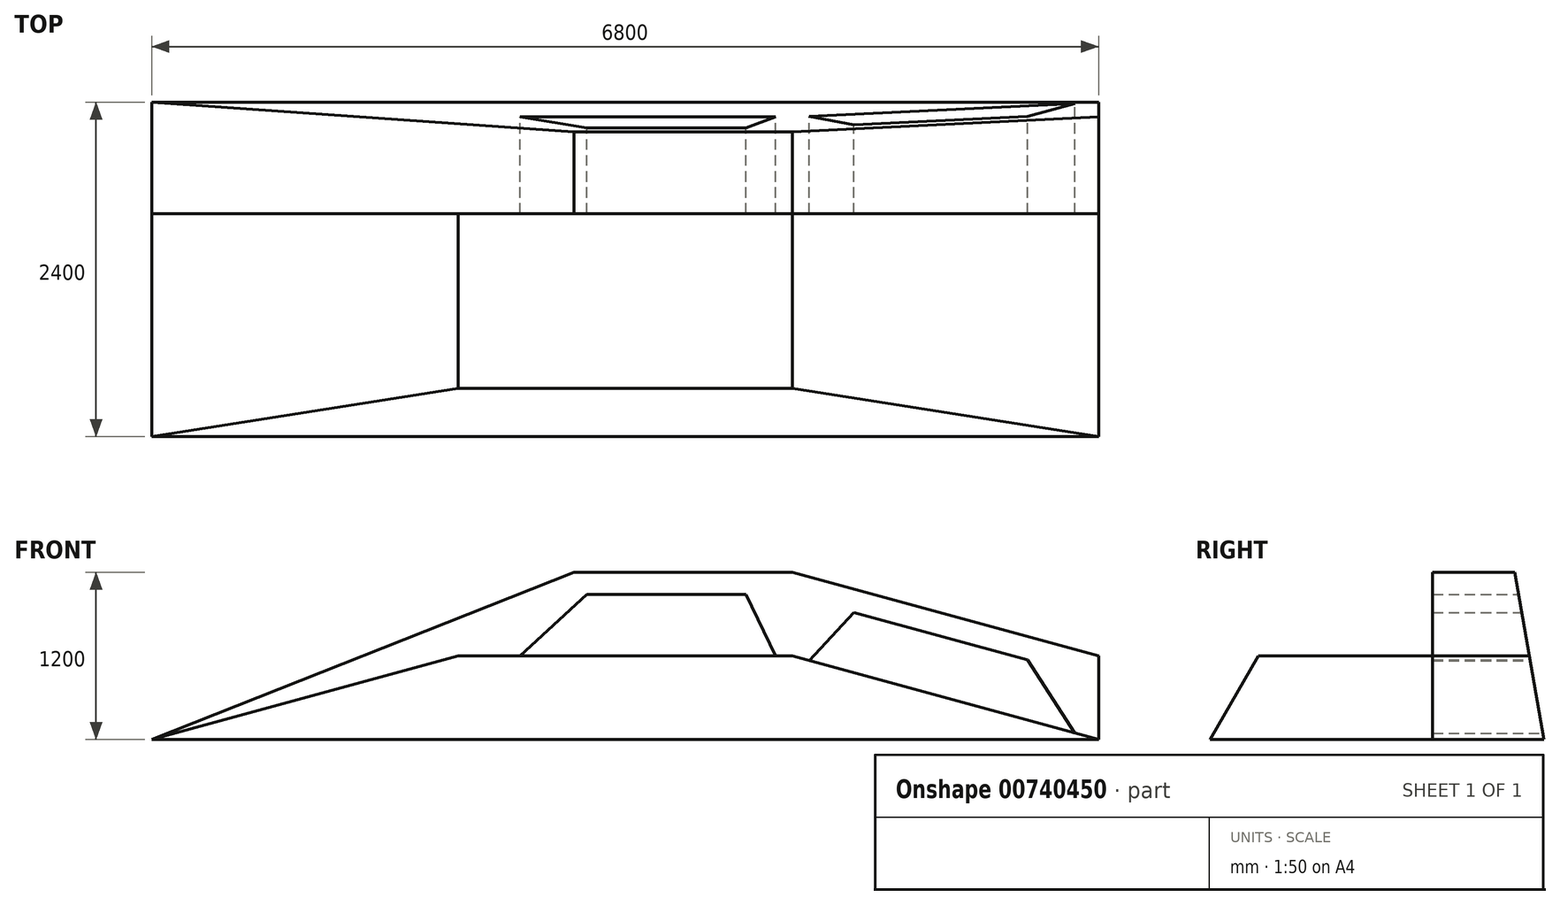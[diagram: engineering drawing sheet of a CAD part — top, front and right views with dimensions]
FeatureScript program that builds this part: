
annotation { "Feature Type Name" : "Feature", "Feature Type Description" : "" }
export const myFeature = defineFeature(function(context is Context, id is Id, definition is map)
    precondition{}
    {
        {
            var Q0;
            Q0=qCreatedBy(makeId("Top.planeOp"),FACE);
            var sketch = newSketch(context, id + "F0", { "sketchPlane" : qUnion([Q0])});
            skLineSegment(sketch, "E0.bottom", {"start": v(3400, 1200) * mm, "end": v(-3400, 1200) * mm});
            skLineSegment(sketch, "E0.top", {"start": v(3400, -1200) * mm, "end": v(-3400, -1200) * mm});
            skLineSegment(sketch, "E0.left", {"start": v(3400, 1200) * mm, "end": v(3400, -1200) * mm});
            skLineSegment(sketch, "E0.right", {"start": v(-3400, 1200) * mm, "end": v(-3400, -1200) * mm});
            skPoint(sketch, "E0.middle", {"position": v(0, 0) * mm});
            skSolve(sketch);
        }
        {
            var Q0;
            Q0=qCreatedBy(makeId("Front.planeOp"),FACE);
            var sketch = newSketch(context, id + "F1", { "sketchPlane" : qUnion([Q0])});
            skPoint(sketch, "E1.orphan", {"position": v(0, 354.61) * mm});
            skLineSegment(sketch, "E2", {"start": v(3400, 0) * mm, "end": v(-3400, 0) * mm});
            skLineSegment(sketch, "E3.MirrorCS", {"start": v(0, 600) * mm, "end": v(0, 1447.26) * mm, "construction": true});
            skLineSegment(sketch, "E4.MirrorCS", {"start": v(1200, 600) * mm, "end": v(3400, 0) * mm});
            skLineSegment(sketch, "E5.MirrorCS", {"start": v(-367.8, 1200) * mm, "end": v(-3400, 0) * mm});
            skLineSegment(sketch, "E6.MirrorCS", {"start": v(-1200, 600) * mm, "end": v(1200, 600) * mm});
            skLineSegment(sketch, "E7.MirrorCS", {"start": v(1200, 1200) * mm, "end": v(3400, 600) * mm});
            skLineSegment(sketch, "E8.MirrorCS", {"start": v(3400, 600) * mm, "end": v(3400, 0) * mm});
            skLineSegment(sketch, "E9.MirrorCS", {"start": v(-367.8, 1200) * mm, "end": v(1200, 1200) * mm});
            skLineSegment(sketch, "E10.MirrorCS", {"start": v(-1200, 600) * mm, "end": v(-3400, 0) * mm});
            skLineSegment(sketch, "E11", {"start": v(-754.09, 600) * mm, "end": v(-276.63, 1039.93) * mm});
            skLineSegment(sketch, "E12", {"start": v(-276.63, 1039.93) * mm, "end": v(1168.64, 1039.93) * mm});
            skLineSegment(sketch, "E13", {"start": v(1168.64, 1039.93) * mm, "end": v(2889.88, 570.5) * mm});
            skLineSegment(sketch, "E14", {"start": v(2889.88, 570.5) * mm, "end": v(3231.45, 45.97) * mm});
            skLineSegment(sketch, "E15", {"start": v(866.56, 1039.93) * mm, "end": v(1080.6, 600) * mm});
            skLineSegment(sketch, "E16", {"start": v(1322.23, 566.67) * mm, "end": v(1641.58, 910.95) * mm});
            skSolve(sketch);
        }
        {
            var Q0;
            Q0=makeQuery(id+"F1.imprint","IMPRINT",FACE,{"disambiguationData":[TD([[makeQuery(id+"F1.imprint","IMPRINT",EDGE,{"derivedFrom":sQuery(id+"F1.wireOp",EDGE,"T3CKHXEt-G5tF-qndR-ku87-O5Xnjiq5KVjb")}),-1.0]])]});
            var Q1;
            Q1=makeQuery(id+"F1.imprint","IMPRINT",FACE,{"disambiguationData":[TD([[makeQuery(id+"F1.imprint","IMPRINT",EDGE,{"derivedFrom":sQuery(id+"F1.wireOp",EDGE,"E5.MirrorCS")}),1.0]])]});
            var Q2;
            {var subQ4=sQuery(id+"F1.wireOp",EDGE,"E15");Q2=makeQuery(id+"F1.imprint","IMPRINT",FACE,{"disambiguationData":[TD([[makeQuery(id+"F1.imprint","IMPRINT",EDGE,{"derivedFrom":subQ4}),1.0]])]});}
            extrude(context, id + "F2", {"entities" : qUnion([Q0, Q1, Q2]), "depth" : 800 * mm, "offsetDistance" : 25 * mm});
        }
        {
            var Q0;
            Q0=makeQuery(id+"F1.imprint","IMPRINT",FACE,{"disambiguationData":[TD([[makeQuery(id+"F1.imprint","IMPRINT",EDGE,{"derivedFrom":sQuery(id+"F1.wireOp",EDGE,"T3CKHXEt-G5tF-qndR-ku87-O5Xnjiq5KVjb")}),1.0]])]});
            var Q1;
            {var subQ4=sQuery(id+"F1.wireOp",EDGE,"E2");Q1=makeQuery(id+"F1.imprint","IMPRINT",FACE,{"disambiguationData":[TD([[makeQuery(id+"F1.imprint","IMPRINT",EDGE,{"derivedFrom":subQ4}),-1.0]])]});}
            extrude(context, id + "F3", {"entities" : qUnion([Q0, Q1]), "operationType" : NewBodyOperationType.ADD, "depth" : 2400 * mm, "offsetDistance" : 25 * mm});
        }
        {
            var Q0;
            Q0=makeQuery(id+"F2.opExtrude","SWEPT_FACE",FACE,{"disambiguationData":[OSD([sQuery(id+"F1.wireOp",EDGE,"E8.MirrorCS")])]});
            var sketch = newSketch(context, id + "F4", { "sketchPlane" : qUnion([Q0])});
            skPoint(sketch, "E17.0", {"position": v(0, 1200) * mm});
            skPoint(sketch, "E18.0", {"position": v(-800, 1200) * mm});
            skPoint(sketch, "E19.0", {"position": v(-800, 0) * mm});
            skPoint(sketch, "E20.0", {"position": v(0, 0) * mm});
            skLineSegment(sketch, "E21", {"start": v(0, 1200) * mm, "end": v(-211.6, 1200) * mm});
            skLineSegment(sketch, "E22", {"start": v(-211.6, 1200) * mm, "end": v(0, 0) * mm});
            skLineSegment(sketch, "E23", {"start": v(0, 1200) * mm, "end": v(0, 0) * mm});
            skPoint(sketch, "E24.0", {"position": v(-2400, 0) * mm});
            skPoint(sketch, "E25.0", {"position": v(-2400, 600) * mm});
            skLineSegment(sketch, "E26", {"start": v(-2400, 0) * mm, "end": v(-2400, 600) * mm});
            skLineSegment(sketch, "E27", {"start": v(-2053.59, 600) * mm, "end": v(-2400, 0) * mm});
            skLineSegment(sketch, "E28", {"start": v(-2400, 600) * mm, "end": v(-2053.59, 600) * mm});
            skSolve(sketch);
        }
        {
            var Q0;
            {var subQ0=sQuery(id+"F4.wireOp",EDGE,"E21");Q0=makeQuery(id+"F4.imprint","IMPRINT",FACE,{"disambiguationData":[TD([[makeQuery(id+"F4.imprint","IMPRINT",EDGE,{"derivedFrom":subQ0}),1.0]])]});}
            var Q1;
            {var subQ0=sQuery(id+"F4.wireOp",EDGE,"E23");var subQ2=sQuery(id+"F1.wireOp",EDGE,"E8.MirrorCS");var subQ6=makeQuery(id+"F2.opExtrude","SWEPT_EDGE",EDGE,{"disambiguationData":[OSD([sQuery(id+"F1.wireOp",EDGE,"E7.MirrorCS"),subQ2])]});var subQ8=makeQuery(id+"F4.imprint","INTERSECT",VERTEX,{"derivedFrom":[subQ6,subQ0]});Q1=makeQuery(id+"F4.imprint","IMPRINT",FACE,{"disambiguationData":[TD([[makeQuery(id+"F4.imprint","IMPRINT",EDGE,{"disambiguationData":[TD([[subQ8,1.0]])],"derivedFrom":subQ6}),-1.0]])]});}
            var Q2;
            Q2=makeQuery(id+"F4.imprint","IMPRINT",FACE,{"disambiguationData":[TD([[makeQuery(id+"F4.imprint","IMPRINT",EDGE,{"derivedFrom":sQuery(id+"F4.wireOp",EDGE,"E26")}),-1.0]])]});
            extrude(context, id + "F5", {"entities" : qUnion([Q0, Q1, Q2]), "operationType" : NewBodyOperationType.REMOVE, "endBound" : BoundingType.THROUGH_ALL, "oppositeDirection" : true, "depth" : 25 * mm, "offsetDistance" : 25 * mm});
        }
    });
